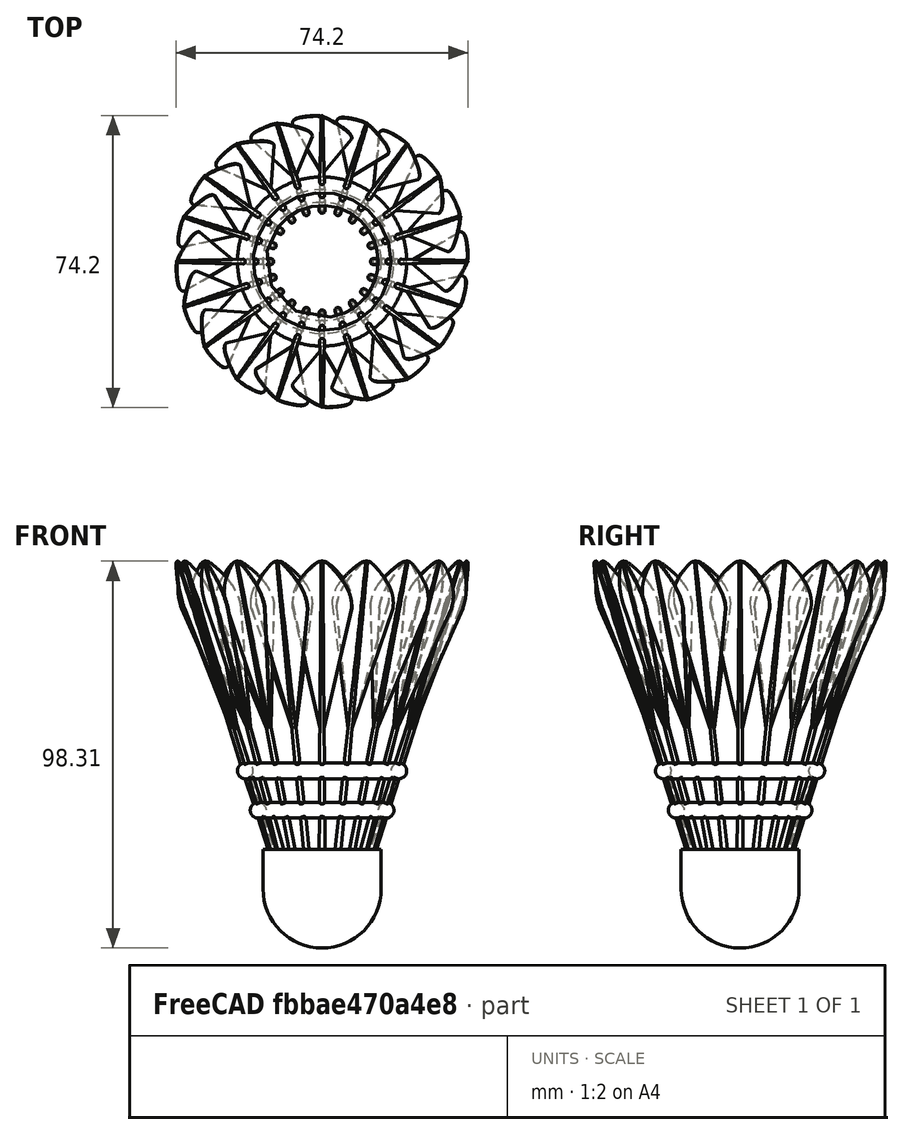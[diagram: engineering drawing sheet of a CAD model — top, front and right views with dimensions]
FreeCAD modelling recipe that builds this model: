
FCSTD DOCUMENT  (FreeCAD 0.21R33771 (Git))
Label: ex36
License: All rights reserved
LicenseURL: https://en.wikipedia.org/wiki/All_rights_reserved
objects: Sketcher::SketchObject×7, PartDesign::Revolution×3, PartDesign::Plane×3, PartDesign::Body×2, PartDesign::Pad×1, PartDesign::AdditiveLoft×1, PartDesign::PolarPattern×1, Part::MultiFuse×1
note: 24 computed .brp shape members not serialized (recipe doc carries the construction recipe); baked Part::Feature solids carry a one-line shape summary decoded from their .brp

FEATURE [Sketcher::SketchObject] Sketch
  FullyConstrained = true
  MapMode = 5
  Placement = pos=(0,0,0) rot=(1,0,0;1.5708rad)
  Support = -> [XZ_Plane]
  sketch-geometry (4):
    g0: LineSegment StartX=0 StartY=0 StartZ=0 EndX=15 EndY=0 EndZ=0
    g1: LineSegment StartX=15 StartY=0 StartZ=0 EndX=15 EndY=-10 EndZ=0
    g2: ArcOfCircle CenterX=-3e-16 CenterY=-10 CenterZ=0 NormalX=0 NormalY=0 NormalZ=1 AngleXU=0 Radius=15 StartAngle=4.71239 EndAngle=6.28319
    g3: LineSegment StartX=0 StartY=0 StartZ=0 EndX=0 EndY=-25 EndZ=0
  constraints (11):
    c: Horizontal(g0)
    c: Coincident(g0,g1)
    c: Vertical(g1)
    c: Tangent(g2,g1) = 1.5708
    c: DistanceX(g0,g0) = 15
    c: DistanceY(g1,g1) = 10
    c: Coincident(g-1,g0)
    c: Coincident(g3,g0)
    c: Coincident(g3,g2)
    c: Tangent(g3,g-2)
    c: Radius(g2) = 15
FEATURE [PartDesign::Revolution] Revolution
  Angle = 360
  Axis = (0,-2e-16,1)
  Base = (0,0,0)
  Placement = pos=(0,0,0) rot=(1,0,0;1.5708rad)
  Profile = -> Sketch
  ReferenceAxis = -> Sketch [V_Axis]
  Reversed = true
FEATURE [PartDesign::Body] Body
  Group = -> [Sketch,Revolution]
  Origin = -> Origin
  Tip = -> Revolution
FEATURE [Sketcher::SketchObject] Sketch001
  FullyConstrained = true
  MapMode = 5
  Placement = pos=(0,0,0) rot=(1,0,0;1.5708rad)
  Support = -> [XZ_Plane001]
  sketch-geometry (1):
    g0: LineSegment StartX=13 StartY=0 StartZ=0 EndX=36.7943 EndY=73.2314 EndZ=0
  constraints (4):
    c: PointOnObject(g0,g-1)
    c: Distance(g0) = 77
    c: DistanceX(g-1,g0) = 13
    c: Angle(g0,g-1) = 1.88496
FEATURE [PartDesign::Plane] DatumPlane
  AttachmentOffset = pos=(0,0,0) rot=(0,-1,0;0.261799rad)
  Length = 152.154
  MapMode = 14
  Placement = pos=(11.7586,-8e-16,-3.8206) rot=(0.711373,0.587166,0.386244;2.12488rad)
  ResizeMode = 0
  Support = -> [Sketch001,Z_Axis001]
  Width = 178.455
FEATURE [PartDesign::Plane] DatumPlane001
  Length = 113.365
  MapMode = 7
  Placement = pos=(36.7943,1.63e-14,73.2314) rot=(0.702714,-0.702714,-0.111299;2.91991rad)
  ResizeMode = 0
  Support = -> [Sketch001]
  Width = 166.794
FEATURE [PartDesign::Plane] DatumPlane002
  Length = 113.365
  MapMode = 7
  Placement = pos=(13,0,0) rot=(0.702714,-0.702714,-0.111299;2.91991rad)
  ResizeMode = 0
  Support = -> [Sketch001]
  Width = 166.794
FEATURE [Sketcher::SketchObject] Sketch002
  ExternalGeometry = -> [Sketch001]
  FullyConstrained = false
  MapMode = 5
  Placement = pos=(11.7586,-4e-16,-3.8206) rot=(0.711373,0.587166,0.386244;2.12488rad)
  Support = -> [DatumPlane]
  sketch-geometry (9):
    g0: ArcOfCircle CenterX=-14.7912 CenterY=61.5414 CenterZ=0 NormalX=0 NormalY=0 NormalZ=1 AngleXU=0 Radius=25 StartAngle=0.584705 EndAngle=0.855928
    g1: ArcOfCircle CenterX=-2.7 CenterY=69.5447 CenterZ=0 NormalX=0 NormalY=0 NormalZ=1 AngleXU=0 Radius=10.5 StartAngle=6.24756 EndAngle=6.86789
    g2: ArcOfCircle CenterX=14.7912 CenterY=61.5414 CenterZ=0 NormalX=0 NormalY=0 NormalZ=1 AngleXU=0 Radius=25 StartAngle=2.28566 EndAngle=2.55689
    g3: ArcOfCircle CenterX=2.7 CenterY=69.5447 CenterZ=0 NormalX=0 NormalY=0 NormalZ=1 AngleXU=0 Radius=10.5 StartAngle=2.55689 EndAngle=3.17722
    g4: LineSegment StartX=-7.79334 StartY=69.1707 StartZ=0 EndX=5.3e-15 EndY=34.0172 EndZ=0
    g5: LineSegment StartX=7.79334 StartY=69.1707 StartZ=0 EndX=5.3e-15 EndY=34.0172 EndZ=0
    g6: GeomPoint X=0 Y=89.9393 Z=0
    g7: ArcOfCircle CenterX=1.76e-14 CenterY=78.5813 CenterZ=0 NormalX=0 NormalY=0 NormalZ=1 AngleXU=0 Radius=2.43589 StartAngle=0.855928 EndAngle=2.28566
    g8: LineSegment StartX=-7.8 StartY=69.5447 StartZ=0 EndX=7.8 EndY=69.5447 EndZ=0
  constraints (21):
    c: Tangent(g1,g0) = -1.5708
    c: Tangent(g3,g2) = -1.5708
    c: Radius(g0) = 25
    c: Radius(g1) = 10.5
    c: Angle(g5,g4) = 0.436332
    c: Coincident(g3,g4)
    c: Coincident(g1,g5)
    c: PointOnObject(g-3,g7)
    c: Symmetric(g2,g0,g-3)
    c: Tangent(g7,g2) = -1.5708
    c: Tangent(g7,g0) = -1.5708
    c: Symmetric(g2,g0,g-3)
    c: Symmetric(g3,g1,g-3)
    c: PointOnObject(g8,g3)
    c: PointOnObject(g8,g1)
    c: Horizontal(g8)
    c: PointOnObject(g1,g8)
    c: DistanceX(g8,g8) = 15.6
    c: Coincident(g4,g5)
    c: DistanceY(g4,g-3) = 47
    c: PointOnObject(g4,g-3)
FEATURE [PartDesign::Pad] Pad
  Direction = (0.91865,-0.258819,-0.298487)
  Length = 0.2
  Length2 = 10
  Midplane = true
  Placement = pos=(11.7586,-8e-16,-3.8206) rot=(0.711373,0.587166,0.386244;2.12488rad)
  Profile = -> Sketch002
  ReferenceAxis = -> Sketch002 [N_Axis]
  Type = 0
FEATURE [Sketcher::SketchObject] Sketch003
  FullyConstrained = true
  MapMode = 5
  Placement = pos=(36.7943,1.63e-14,73.2314) rot=(0.702714,-0.702714,-0.111299;2.91991rad)
  Support = -> [DatumPlane001]
  sketch-geometry (1):
    g0: Circle CenterX=0 CenterY=0 CenterZ=0 NormalX=0 NormalY=0 NormalZ=1 AngleXU=0 Radius=0.25
  constraints (2):
    c: Coincident(g0,g-1)
    c: Radius(g0) = 0.25
FEATURE [Sketcher::SketchObject] Sketch004
  FullyConstrained = true
  MapMode = 5
  Placement = pos=(13,0,4e-16) rot=(0.702714,-0.702714,-0.111299;2.91991rad)
  Support = -> [DatumPlane002]
  sketch-geometry (1):
    g0: Circle CenterX=0 CenterY=0 CenterZ=0 NormalX=0 NormalY=0 NormalZ=1 AngleXU=0 Radius=0.75
  constraints (2):
    c: Coincident(g0,g-1)
    c: Radius(g0) = 0.75
FEATURE [PartDesign::AdditiveLoft] AdditiveLoft
  BaseFeature = -> Pad
  Closed = false
  Placement = pos=(11.7586,-8e-16,-3.8206) rot=(0.711373,0.587166,0.386244;2.12488rad)
  Profile = -> Sketch004
  Ruled = false
  Sections = -> [Sketch003]
FEATURE [Sketcher::SketchObject] Sketch005
  ExternalGeometry = -> [Sketch001]
  FullyConstrained = true
  MapMode = 5
  Placement = pos=(0,0,0) rot=(1,0,0;1.5708rad)
  Support = -> [XZ_Plane001]
  sketch-geometry (1):
    g0: Circle CenterX=16.2492 CenterY=10 CenterZ=0 NormalX=0 NormalY=0 NormalZ=1 AngleXU=0 Radius=2
  constraints (3):
    c: PointOnObject(g0,g-3)
    c: Radius(g0) = 2
    c: DistanceY(g-1,g0) = 10
FEATURE [PartDesign::Revolution] Revolution001
  Angle = 360
  Axis = (0,2e-16,1)
  Base = (0,0,0)
  BaseFeature = -> AdditiveLoft
  Placement = pos=(11.7586,-8e-16,-3.8206) rot=(0.711373,0.587166,0.386244;2.12488rad)
  Profile = -> Sketch005
  ReferenceAxis = -> Sketch005 [V_Axis]
  Reversed = true
FEATURE [Sketcher::SketchObject] Sketch006
  ExternalGeometry = -> [Sketch001]
  FullyConstrained = true
  MapMode = 5
  Placement = pos=(0,0,0) rot=(1,0,0;1.5708rad)
  Support = -> [XZ_Plane001]
  sketch-geometry (1):
    g0: Circle CenterX=19.4984 CenterY=20 CenterZ=0 NormalX=0 NormalY=0 NormalZ=1 AngleXU=0 Radius=2
  constraints (3):
    c: PointOnObject(g0,g-3)
    c: Radius(g0) = 2
    c: DistanceY(g-1,g0) = 20
FEATURE [PartDesign::Revolution] Revolution002
  Angle = 360
  Axis = (0,2e-16,1)
  Base = (0,0,0)
  BaseFeature = -> Revolution001
  Placement = pos=(11.7586,-8e-16,-3.8206) rot=(0.711373,0.587166,0.386244;2.12488rad)
  Profile = -> Sketch006
  ReferenceAxis = -> Sketch006 [V_Axis]
  Reversed = true
FEATURE [PartDesign::PolarPattern] PolarPattern
  Angle = 360
  Axis = -> Z_Axis001
  BaseFeature = -> Revolution002
  Occurrences = 20
  Originals = -> [Pad,AdditiveLoft]
  Placement = pos=(11.7586,-8e-16,-3.8206) rot=(0.711373,0.587166,0.386244;2.12488rad)
FEATURE [PartDesign::Body] Body001
  Group = -> [Sketch001,DatumPlane,DatumPlane001,DatumPlane002,Sketch002,Pad,Sketch003,Sketch004,AdditiveLoft,Sketch005,Revolution001,Sketch006,Revolution002,PolarPattern]
  Origin = -> Origin001
  Tip = -> PolarPattern
FEATURE [Part::MultiFuse] Fusion
  Shapes = -> [Body,Body001]
